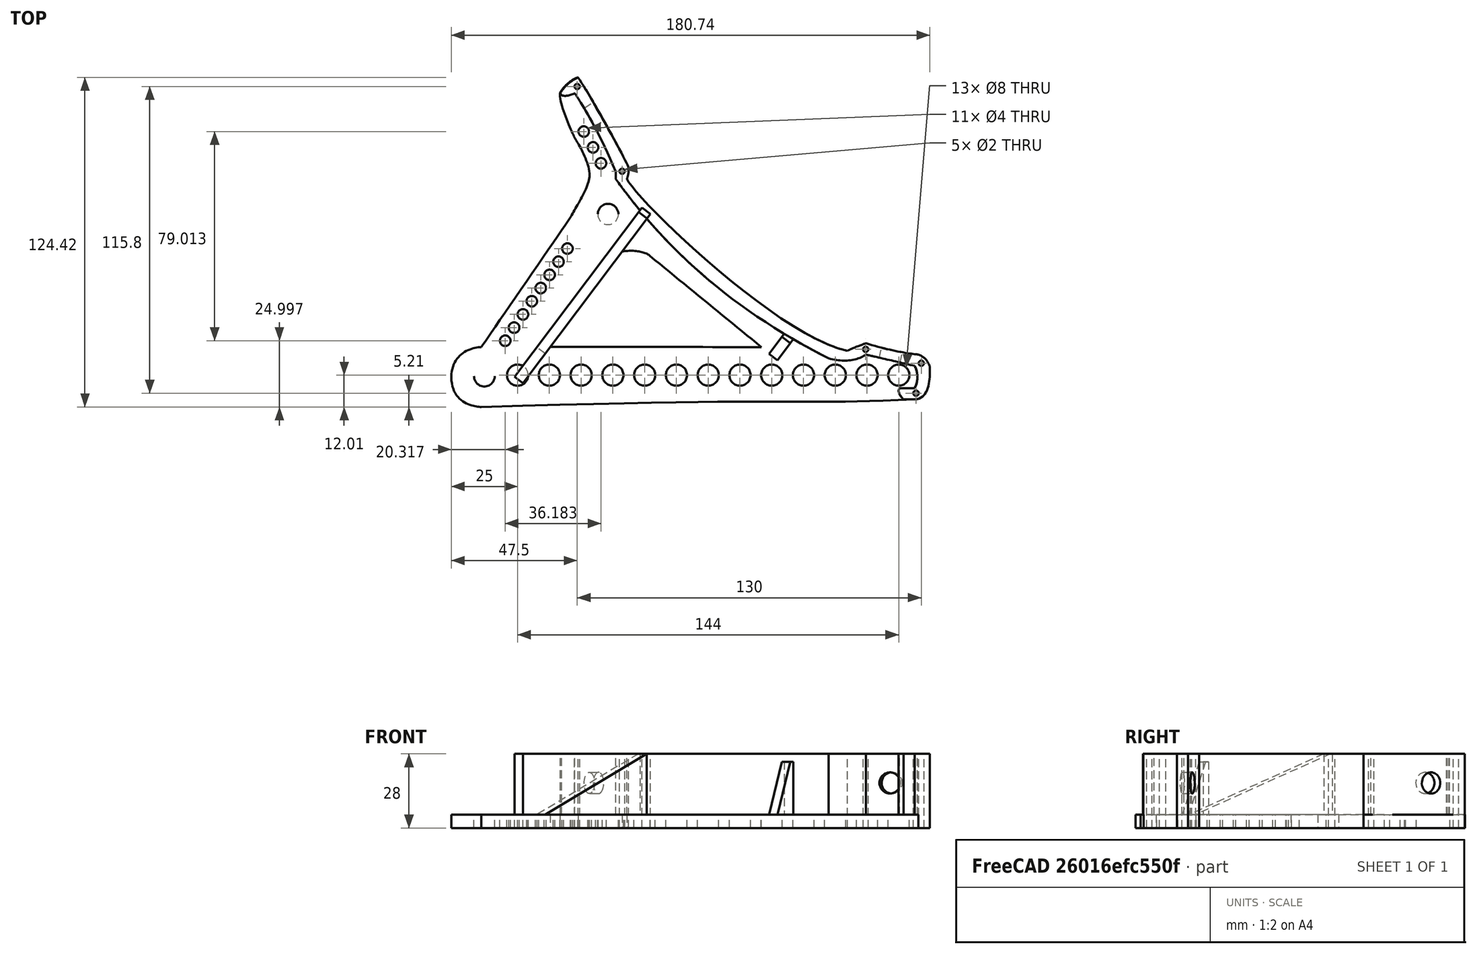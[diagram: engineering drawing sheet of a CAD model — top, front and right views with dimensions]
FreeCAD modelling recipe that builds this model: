
FCSTD DOCUMENT  (FreeCAD 0.15R4503 (Git))
Label: licenseplate_holder
License: CC-BY 3.0
LicenseURL: http://creativecommons.org/licenses/by/3.0/
objects: Part::Cylinder×12, Part::Feature×6, Part::Extrusion×5, Part::FeaturePython×2, Part::Cut×2, Part::MultiFuse×2, Part::Box×1, Sketcher::SketchObject×1, PartDesign::Pocket×1
note: 33 computed .brp shape members not serialized (recipe doc carries the construction recipe); baked Part::Feature solids carry a one-line shape summary decoded from their .brp

FEATURE [Part::Cylinder] Cylinder
  Angle = 360
  Height = 10
  Placement = pos=(25,-134,-1) rot=(0,0,1;0rad)
  Radius = 4
FEATURE [Part::FeaturePython] Array  # Draft array (typed FeaturePython)
  Angle = 360
  ArrayType = 0
  Axis = (0,0,1)
  Base = -> Cylinder
  Center = (0,0,0)
  IntervalAxis = (0,0,0)
  IntervalX = (12,0,0)
  IntervalY = (0,1,0)
  IntervalZ = (0,0,0)
  NumberPolar = 1
  NumberX = 13
  NumberY = 1
  NumberZ = 1
FEATURE [Part::Cylinder] Cylinder001
  Angle = 360
  Height = 10
  Placement = pos=(21,-120,0) rot=(0,0,1;0rad)
  Radius = 2
FEATURE [Part::FeaturePython] Array001  # Draft array (typed FeaturePython)
  Angle = 360
  ArrayType = 0
  Axis = (0,0,1)
  Base = -> Cylinder001
  Center = (0,0,0)
  IntervalAxis = (0,0,0)
  IntervalX = (6,0,0)
  IntervalY = (0,1,0)
  IntervalZ = (0,0,0)
  NumberPolar = 1
  NumberX = 8
  NumberY = 1
  NumberZ = 1
  Placement = pos=(-90.8982,-71.2913,0) rot=(0,0,1;0.97713rad)
FEATURE [Part::Feature] Pocket001
  Placement = pos=(122,-130,0) rot=(0,0,1;0.925025rad)
  shape: bbox 10.42 x 11.99 x 25 mm, 6 faces (baked)
FEATURE [Part::Cylinder] Cylinder002
  Angle = 360
  Height = 30
  Placement = pos=(64.5,-57,0) rot=(0,0,1;0rad)
  Radius = 1
FEATURE [Part::Cylinder] Cylinder003
  Angle = 360
  Height = 30
  Placement = pos=(47.5,-25,0) rot=(0,0,1;0rad)
  Radius = 1
FEATURE [Part::Cylinder] Cylinder004
  Angle = 360
  Height = 30
  Placement = pos=(156.5,-124.25,0) rot=(0,0,1;0rad)
  Radius = 1
FEATURE [Part::Cylinder] Cylinder005
  Angle = 360
  Height = 30
  Placement = pos=(177.5,-129.5,0) rot=(0,0,1;0rad)
  Radius = 1
FEATURE [Part::Cylinder] Cylinder006
  Angle = 360
  Height = 30
  Placement = pos=(175.5,-140.8,0) rot=(0,0,1;0rad)
  Radius = 1
FEATURE [Part::Cylinder] Cylinder007
  Angle = 360
  Height = 10
  Placement = pos=(50,-42,0) rot=(0,0,1;0rad)
  Radius = 2
FEATURE [Part::Cylinder] Cylinder008
  Angle = 360
  Height = 10
  Placement = pos=(53.5,-48,0) rot=(0,0,1;0rad)
  Radius = 2
FEATURE [Part::Cylinder] Cylinder009
  Angle = 360
  Height = 10
  Placement = pos=(56.5,-54,0) rot=(0,0,1;0rad)
  Radius = 2
FEATURE [Part::Cylinder] Cylinder010
  Angle = 360
  Height = 18
  Placement = pos=(50,-38,17) rot=(-0.544988,0.838444,0;1.5708rad)
  Radius = 4
FEATURE [Part::Cylinder] Cylinder011
  Angle = 360
  Height = 18
  Placement = pos=(164,-136,17) rot=(-0.97873,0.205153,0;1.5708rad)
  Radius = 4
FEATURE [Part::Feature] path3077
  shape: bbox 7.805 x 7.805 x 2e-07 mm, 0 faces, 0 solids (baked)
FEATURE [Part::Feature] path3079
  shape: bbox 7.807 x 7.807 x 2e-07 mm, 0 faces, 0 solids (baked)
FEATURE [Part::Feature] path3083
  shape: bbox 83.99 x 37.1 x 2e-07 mm, 0 faces, 0 solids (baked)
FEATURE [Part::Feature] path3083001
  shape: bbox 182 x 124.4 x 2e-07 mm, 0 faces, 0 solids (baked)
FEATURE [Part::Feature] path3083_5
  shape: bbox 140.9 x 121.5 x 2e-07 mm, 0 faces, 0 solids (baked)
FEATURE [Part::Extrusion] Extrude
  Base = -> path3083001
  Dir = (0,0,5)
  Solid = true
FEATURE [Part::Extrusion] Extrude001
  Base = -> path3077
  Dir = (0,0,5)
  Solid = true
FEATURE [Part::Extrusion] Extrude002
  Base = -> path3079
  Dir = (0,0,5)
  Solid = true
FEATURE [Part::Extrusion] Extrude003
  Base = -> path3083
  Dir = (0,0,5)
  Solid = true
FEATURE [Part::Extrusion] Extrude004
  Base = -> path3083_5
  Dir = (0,0,28)
  Solid = true
FEATURE [Part::Box] Box  label="Cube"
  Height = 28
  Length = 80
  Placement = pos=(27,-137,0) rot=(0,0,1;0.925025rad)
  Width = 4
FEATURE [Sketcher::SketchObject] Sketch
  Placement = pos=(23.8055,-134.593,0) rot=(-0.332492,0.666877,0.666877;3.78358rad)
  Support = -> Box [Face4]
  sketch-geometry (5):
    g0: LineSegment StartX=-78.1016 StartY=28.0753 StartZ=0 EndX=0 EndY=0 EndZ=0
    g1: LineSegment StartX=0 StartY=0 StartZ=0 EndX=10 EndY=0 EndZ=0
    g2: LineSegment StartX=10 StartY=0 StartZ=0 EndX=10 EndY=35.4286 EndZ=0
    g3: LineSegment StartX=10 StartY=35.4286 StartZ=0 EndX=-74.6742 EndY=35.4286 EndZ=0
    g4: LineSegment StartX=-74.6742 StartY=35.4286 StartZ=0 EndX=-78.1016 EndY=28.0753 EndZ=0
  constraints (9):
    c: Coincident(g0,g-1)
    c: Coincident(g0,g1)
    c: Horizontal(g1)
    c: Coincident(g1,g2)
    c: Vertical(g2)
    c: Coincident(g2,g3)
    c: Horizontal(g3)
    c: Coincident(g3,g4)
    c: Coincident(g4,g0)
FEATURE [PartDesign::Pocket] Pocket
  Length = 5
  Placement = pos=(27,-137,0) rot=(0,0,1;0.925025rad)
  Sketch = -> Sketch
  Type = 0
FEATURE [Part::Cut] Cut
  Base = -> Extrude
  Tool = -> Extrude003
FEATURE [Part::MultiFuse] Fusion
  Shapes = -> [Cut,Pocket,Pocket001,Extrude004]
FEATURE [Part::MultiFuse] Fusion001
  Shapes = -> [Cylinder010,Array,Array001,Cylinder002,Cylinder003,Cylinder004,Cylinder005,Cylinder006,Cylinder007,Cylinder008,Cylinder009,Cylinder011,Extrude002,Extrude001]
FEATURE [Part::Cut] Cut001
  Base = -> Fusion
  Tool = -> Fusion001
